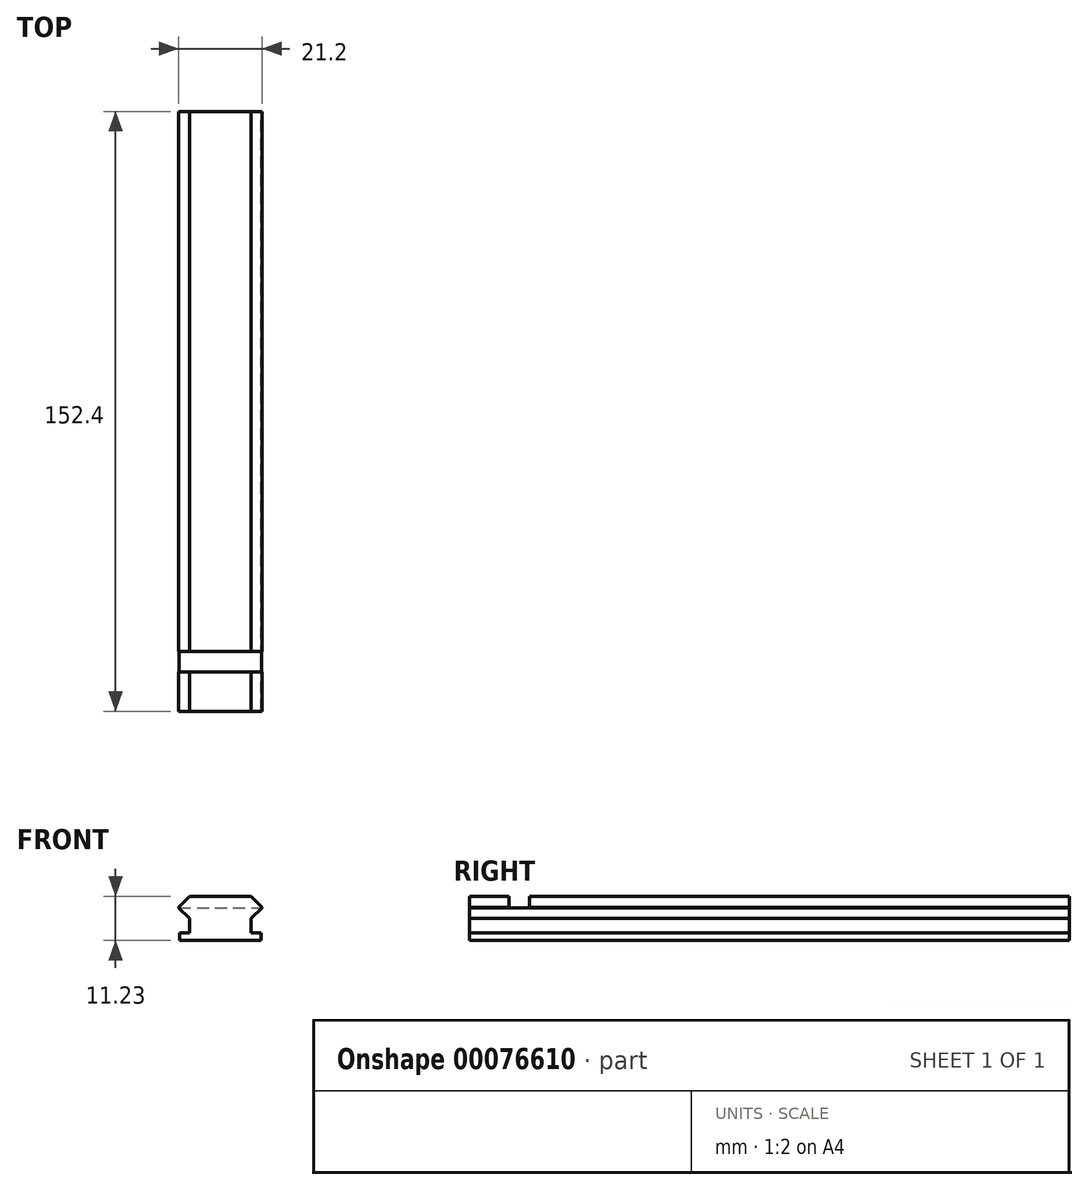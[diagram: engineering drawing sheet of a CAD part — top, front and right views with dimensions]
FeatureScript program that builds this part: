
annotation { "Feature Type Name" : "Feature", "Feature Type Description" : "" }
export const myFeature = defineFeature(function(context is Context, id is Id, definition is map)
    precondition{}
    {
        {
            var Q0;
            Q0=qCreatedBy(makeId("Front.planeOp"),FACE);
            var sketch = newSketch(context, id + "F0", { "sketchPlane" : qUnion([Q0])});
            skLineSegment(sketch, "E0", {"start": v(0, 0) * mm, "end": v(7.84, 0) * mm});
            skLineSegment(sketch, "E1", {"start": v(7.84, 0) * mm, "end": v(10.6, -2.77) * mm});
            skLineSegment(sketch, "E2", {"start": v(10.6, -2.77) * mm, "end": v(10.6, -2.9) * mm});
            skLineSegment(sketch, "E3", {"start": v(10.6, -2.9) * mm, "end": v(7.84, -5.67) * mm});
            skLineSegment(sketch, "E4", {"start": v(7.84, -5.67) * mm, "end": v(7.84, -9.32) * mm});
            skLineSegment(sketch, "E5", {"start": v(7.84, -9.32) * mm, "end": v(10.32, -9.32) * mm});
            skLineSegment(sketch, "E6", {"start": v(10.32, -9.32) * mm, "end": v(10.32, -11.23) * mm});
            skLineSegment(sketch, "E7", {"start": v(10.32, -11.23) * mm, "end": v(0, -11.23) * mm});
            skLineSegment(sketch, "E8", {"start": v(0, -11.23) * mm, "end": v(0, 0) * mm});
            skLineSegment(sketch, "E9", {"start": v(9.5, -1.66) * mm, "end": v(0, -1.66) * mm});
            skLineSegment(sketch, "E10", {"start": v(9.34, -4.17) * mm, "end": v(0, -4.17) * mm});
            skLineSegment(sketch, "E11.MirrorCS", {"start": v(0, 0) * mm, "end": v(-7.84, 0) * mm});
            skLineSegment(sketch, "E12.MirrorCS", {"start": v(-7.84, 0) * mm, "end": v(-10.6, -2.77) * mm});
            skLineSegment(sketch, "E13.MirrorCS", {"start": v(-10.6, -2.9) * mm, "end": v(-7.84, -5.67) * mm});
            skLineSegment(sketch, "E14.MirrorCS", {"start": v(-10.6, -2.77) * mm, "end": v(-10.6, -2.9) * mm});
            skLineSegment(sketch, "E15.MirrorCS", {"start": v(-7.84, -5.67) * mm, "end": v(-7.84, -9.32) * mm});
            skLineSegment(sketch, "E16.MirrorCS", {"start": v(-10.32, -9.32) * mm, "end": v(-10.32, -11.23) * mm});
            skLineSegment(sketch, "E17.MirrorCS", {"start": v(-10.32, -11.23) * mm, "end": v(0, -11.23) * mm});
            skLineSegment(sketch, "E18.MirrorCS", {"start": v(-7.84, -9.32) * mm, "end": v(-10.32, -9.32) * mm});
            skLineSegment(sketch, "E19.MirrorCS", {"start": v(-9.5, -1.66) * mm, "end": v(0, -1.66) * mm});
            skLineSegment(sketch, "E20.MirrorCS", {"start": v(-9.34, -4.17) * mm, "end": v(0, -4.17) * mm});
            skSolve(sketch);
        }
        {
            var Q0;
            {var subQ4=sQuery(id+"F0.wireOp",EDGE,"E2");Q0=makeQuery(id+"F0.imprint","IMPRINT",FACE,{"disambiguationData":[TD([[makeQuery(id+"F0.imprint","IMPRINT",EDGE,{"derivedFrom":subQ4}),-1.0]])]});}
            var Q1;
            {var subQ1=sQuery(id+"F0.wireOp",EDGE,"E15.MirrorCS");Q1=makeQuery(id+"F0.imprint","IMPRINT",FACE,{"disambiguationData":[TD([[makeQuery(id+"F0.imprint","IMPRINT",EDGE,{"derivedFrom":subQ1}),1.0]])]});}
            var Q2;
            {var subQ1=sQuery(id+"F0.wireOp",EDGE,"E4");Q2=makeQuery(id+"F0.imprint","IMPRINT",FACE,{"disambiguationData":[TD([[makeQuery(id+"F0.imprint","IMPRINT",EDGE,{"derivedFrom":subQ1}),-1.0]])]});}
            var Q3;
            {var subQ0=sQuery(id+"F0.wireOp",EDGE,"E14.MirrorCS");Q3=makeQuery(id+"F0.imprint","IMPRINT",FACE,{"disambiguationData":[TD([[makeQuery(id+"F0.imprint","IMPRINT",EDGE,{"derivedFrom":subQ0}),1.0]])]});}
            var Q4;
            {var subQ0=sQuery(id+"F0.wireOp",EDGE,"E11.MirrorCS");Q4=makeQuery(id+"F0.imprint","IMPRINT",FACE,{"disambiguationData":[TD([[makeQuery(id+"F0.imprint","IMPRINT",EDGE,{"derivedFrom":subQ0}),1.0]])]});}
            var Q5;
            {var subQ0=sQuery(id+"F0.wireOp",EDGE,"E0");Q5=makeQuery(id+"F0.imprint","IMPRINT",FACE,{"disambiguationData":[TD([[makeQuery(id+"F0.imprint","IMPRINT",EDGE,{"derivedFrom":subQ0}),-1.0]])]});}
            extrude(context, id + "F1", {"entities" : qUnion([Q0, Q1, Q2, Q3, Q4, Q5]), "depth" : 152.4 * mm});
        }
        {
            var Q0;
            Q0=makeQuery(id+"F1.opExtrude","SWEPT_FACE",FACE,{"disambiguationData":[OSD([sQuery(id+"F0.wireOp",EDGE,"E0"),sQuery(id+"F0.wireOp",EDGE,"E11.MirrorCS")])]});
            cPlane(context, id + "F2", {"entities" : qUnion([Q0]), "cplaneType" : CPlaneType.OFFSET, "offset" : 3 * mm, "oppositeDirection" : true, "width" : 152.4 * mm, "height" : 152.4 * mm});
        }
        {
            var Q0;
            Q0=qCreatedBy(id+"F2.planeOp",FACE);
            var sketch = newSketch(context, id + "F3", { "sketchPlane" : qUnion([Q0])});
            skLineSegment(sketch, "E21.bottom", {"start": v(-10.6, -142.4) * mm, "end": v(10.6, -142.4) * mm});
            skLineSegment(sketch, "E21.top", {"start": v(-10.6, -137.16) * mm, "end": v(10.6, -137.16) * mm});
            skLineSegment(sketch, "E21.left", {"start": v(-10.6, -142.4) * mm, "end": v(-10.6, -137.16) * mm});
            skLineSegment(sketch, "E21.right", {"start": v(10.6, -142.4) * mm, "end": v(10.6, -137.16) * mm});
            skSolve(sketch);
        }
        {
            var Q0;
            Q0 = qSketchRegion(id + "F3", true);
            extrude(context, id + "F4", {"entities" : qUnion([Q0]), "operationType" : NewBodyOperationType.REMOVE, "depth" : 3 * mm});
        }
    });
